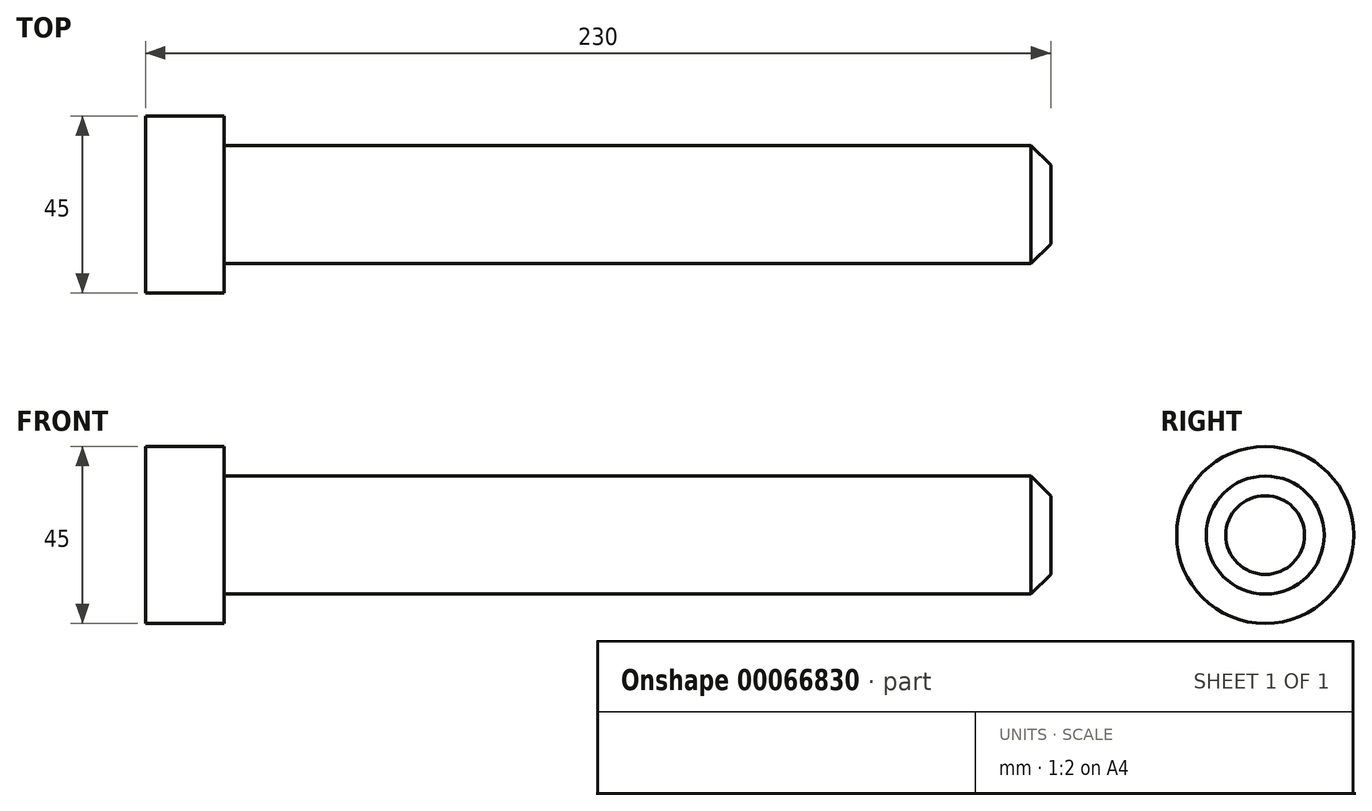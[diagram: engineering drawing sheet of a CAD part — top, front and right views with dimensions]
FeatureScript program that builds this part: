
annotation { "Feature Type Name" : "Feature", "Feature Type Description" : "" }
export const myFeature = defineFeature(function(context is Context, id is Id, definition is map)
    precondition{}
    {
        {
            var Q0;
            Q0=qCreatedBy(makeId("Front.planeOp"),FACE);
            var sketch = newSketch(context, id + "F0", { "sketchPlane" : qUnion([Q0])});
            skLineSegment(sketch, "E0", {"start": v(-20, 0) * mm, "end": v(-20, 22.5) * mm});
            skLineSegment(sketch, "E1", {"start": v(-20, 22.5) * mm, "end": v(0, 22.5) * mm});
            skLineSegment(sketch, "E2", {"start": v(0, 22.5) * mm, "end": v(0, 15) * mm});
            skLineSegment(sketch, "E3", {"start": v(0, 15) * mm, "end": v(210, 15) * mm});
            skLineSegment(sketch, "E4", {"start": v(210, 15) * mm, "end": v(210, 0) * mm});
            skLineSegment(sketch, "E5", {"start": v(210, 0) * mm, "end": v(-20, 0) * mm});
            skSolve(sketch);
        }
        {
            var Q0;
            Q0=makeQuery(id+"F0.imprint","IMPRINT",FACE,{"disambiguationData":[TD([[makeQuery(id+"F0.imprint","IMPRINT",EDGE,{"derivedFrom":sQuery(id+"F0.wireOp",EDGE,"E0")}),-1.0]])]});
            var Q1;
            Q1=sQuery(id+"F0.wireOp",EDGE,"E5");
            revolve(context, id + "F1", {"entities" : qUnion([Q0]), "axis" : qUnion([Q1]), "revolveType" : RevolveType.FULL});
        }
        {
            var Q0;
            Q0=makeQuery(id+"F1.opRevolve","SWEPT_EDGE",EDGE,{"disambiguationData":[OSD([sQuery(id+"F0.wireOp",EDGE,"E3"),sQuery(id+"F0.wireOp",EDGE,"E4")])]});
            chamfer(context, id + "F2", {"entities" : qUnion([Q0]), "width" : 5 * mm, "tangentPropagation" : true});
        }
    });
